# Revit family: WATER-SOLENOID-VALVE
name_source: partatom
category: Pipe Accessories
units: mm (PartAtom-declared; Revit-internal decimal feet)

## family parameters
Always vertical = Yes
Cut with Voids When Loaded = No
Part Type = Valve - Breaks Into
Round Connector Dimension = Use Diameter
Shared = No
Work Plane-Based = No

## types (24) — shared parameters
ARMATURE TUBE = Stainless Steel 300
Body material = Lead Free Brass
Coil class = F
Coil type = D
Default Elevation = 0.00"
FIXED CORE = Stainless Steel 400
Frequency Hz for 120VAC / 24VAC = 50/60
Frequency Hz for 24VDC = DC
Manufacturer = American Gas Safety LLC
ORIFICE = Lead Free Brass
PLUNGER = Stainless Steel 400
Popular Applications = Schools, Laboratories, Residential, Hospitals
, Drinking Water Control
Power (VA) for 120VAC / 24VAC = 20
Power (W) for 24VDC = 17 W
Rating = Nema 4
SHADING RING = Copper
SPRING = Stainless Steel 300
Tel = (727) 608-4375
URL = https://americangassafety.com

## per-type parameters (varying)
| type | 1 1/2'' | 1 1/4'' | 1'' | 1/2'' | 2'' | 3/4'' | ABOVE 1 1/4'' | BELOW 1 1/4'' | BIG BOLTS | Description | ID | LENGTH | MEDIUM BOLTS 1 | MEDIUM BOLTS 2 | SMALL BOLTS | Volt |
| SOLVLVNC12 | No | No | No | Yes | No | No | No | Yes | No | AGS water solenoid valves are normally closed (N/C) and constructed with a durable lead free brass body, two-way inlet and outlet ports. | 0.50" | 2.59" | No | No | Yes | 120VAC |
| SOLVLV12NC-24V | No | No | No | Yes | No | No | No | Yes | No | AGS water solenoid valves are normally closed (N/C) and constructed with a durable lead free brass body, two-way inlet and outlet ports. | 0.50" | 2.59" | No | No | Yes | 24VDC & 24VAC |
| SOLVLVNC34 | No | No | No | No | No | Yes | No | Yes | No | AGS water solenoid valves are normally closed (N/C) and constructed with a durable lead free brass body, two-way inlet and outlet ports. | 0.75" | 2.95" | No | No | Yes | 120VAC |
| SOLVLV34NC-24V | No | No | No | No | No | Yes | No | Yes | No | AGS water solenoid valves are normally closed (N/C) and constructed with a durable lead free brass body, two-way inlet and outlet ports. | 0.75" | 2.95" | No | No | Yes | 24VDC & 24VAC |
| SOLVLVNC1 | No | No | Yes | No | No | No | No | Yes | No | AGS water solenoid valves are normally closed (N/C) and constructed with a durable lead free brass body, two-way inlet and outlet ports. | 1.00" | 3.78" | Yes | No | No | 120VAC |
| SOLVLV1NC-24V | No | No | Yes | No | No | No | No | Yes | No | AGS water solenoid valves are normally closed (N/C) and constructed with a durable lead free brass body, two-way inlet and outlet ports. | 1.00" | 3.78" | Yes | No | No | 24VDC & 24VAC |
| SOLVLVNC114 | No | Yes | No | No | No | No | Yes | No | No | AGS water solenoid valves are normally closed (N/C) and constructed with a durable lead free brass body, two-way inlet and outlet ports. | 1.25" | 5.16" | No | Yes | No | 120VAC |
| SOLVLV114NC-24V | No | Yes | No | No | No | No | Yes | No | No | AGS water solenoid valves are normally closed (N/C) and constructed with a durable lead free brass body, two-way inlet and outlet ports. | 1.25" | 5.16" | No | Yes | No | 24VDC & 24VAC |
| SOLVLVNC112 | Yes | No | No | No | No | No | Yes | No | No | AGS water solenoid valves are normally closed (N/C) and constructed with a durable lead free brass body, two-way inlet and outlet ports. | 1.50" | 5.16" | No | Yes | No | 120VAC |
| SOLVLV112NC-24V | Yes | No | No | No | No | No | Yes | No | No | AGS water solenoid valves are normally closed (N/C) and constructed with a durable lead free brass body, two-way inlet and outlet ports. | 1.50" | 5.16" | No | Yes | No | 24VDC & 24VAC |
| SOLVLVNC2 | No | No | No | No | Yes | No | Yes | No | Yes | AGS water solenoid valves are normally closed (N/C) and constructed with a durable lead free brass body, two-way inlet and outlet ports. | 2.00" | 6.50" | No | No | No | 120VAC |
| SOLVLV2NC-24V | No | No | No | No | Yes | No | Yes | No | Yes | AGS water solenoid valves are normally closed (N/C) and constructed with a durable lead free brass body, two-way inlet and outlet ports. | 2.00" | 6.50" | No | No | No | 24VDC & 24VAC |
| SOLVLVNO12 | No | No | No | Yes | No | No | No | Yes | No | AGS water solenoid valves are normally open (N/O) and constructed with a durable lead free brass body, two-way inlet and outlet ports. | 0.50" | 2.59" | No | No | Yes | 120VAC |
| SOLVLV12NO-24V | No | No | No | Yes | No | No | No | Yes | No | AGS wAGS water solenoid valves are normally open (N/O) and constructed with a durable lead free brass body, two-way inlet and outlet ports.ater solenoid valves are normally closed (N/C) and constructed with a durable lead free brass body, two-way inlet and outlet ports. | 0.50" | 2.59" | No | No | Yes | 24VDC & 24VAC |
| SOLVLVNO34 | No | No | No | No | No | Yes | No | Yes | No | AGS water solenoid valves are normally open (N/O) and constructed with a durable lead free brass body, two-way inlet and outlet ports. | 0.75" | 2.95" | No | No | Yes | 120VAC |
| SOLVLV34NO-24V | No | No | No | No | No | Yes | No | Yes | No | AGS water solenoid valves are normally open (N/O) and constructed with a durable lead free brass body, two-way inlet and outlet ports. | 0.75" | 2.95" | No | No | Yes | 24VDC & 24VAC |
| SOLVLVNO1 | No | No | Yes | No | No | No | No | Yes | No | AGS water solenoid valves are normally open (N/O) and constructed with a durable lead free brass body, two-way inlet and outlet ports. | 1.00" | 3.78" | Yes | No | No | 120VAC |
| SOLVLV1NO-24V | No | No | Yes | No | No | No | No | Yes | No | AGS water solenoid valves are normally open (N/O) and constructed with a durable lead free brass body, two-way inlet and outlet ports. | 1.00" | 3.78" | Yes | No | No | 24VDC & 24VAC |
| SOLVLVNO114 | No | Yes | No | No | No | No | Yes | No | No | AGS water solenoid valves are normally open (N/O) and constructed with a durable lead free brass body, two-way inlet and outlet ports. | 1.25" | 5.16" | No | Yes | No | 120VAC |
| SOLVLV114NO-24V | No | Yes | No | No | No | No | Yes | No | No | AGS water solenoid valves are normally open (N/O) and constructed with a durable lead free brass body, two-way inlet and outlet ports. | 1.25" | 5.16" | No | Yes | No | 24VDC & 24VAC |
| SOLVLVNO112 | Yes | No | No | No | No | No | Yes | No | No | AGS water solenoid valves are normally open (N/O) and constructed with a durable lead free brass body, two-way inlet and outlet ports. | 1.50" | 5.16" | No | Yes | No | 120VAC |
| SOLVLV112NO-24V | Yes | No | No | No | No | No | Yes | No | No | AGS water solenoid valves are normally open (N/O) and constructed with a durable lead free brass body, two-way inlet and outlet ports. | 1.50" | 5.16" | No | Yes | No | 24VDC & 24VAC |
| SOLVLVNO2 | No | No | No | No | Yes | No | Yes | No | Yes | AGS water solenoid valves are normally open (N/O) and constructed with a durable lead free brass body, two-way inlet and outlet ports. | 2.00" | 6.50" | No | No | No | 120VAC |
| SOLVLV2NO-24V | No | No | No | No | Yes | No | Yes | No | Yes | AGS water solenoid valves are normally open (N/O) and constructed with a durable lead free brass body, two-way inlet and outlet ports. | 2.00" | 6.50" | No | No | No | 24VDC & 24VAC |

note: column(s) folded — value = type name in every type: Model

## geometry (parser evidence)
native form markers: Sweep x3
no freeform markers — native parametric forms only
